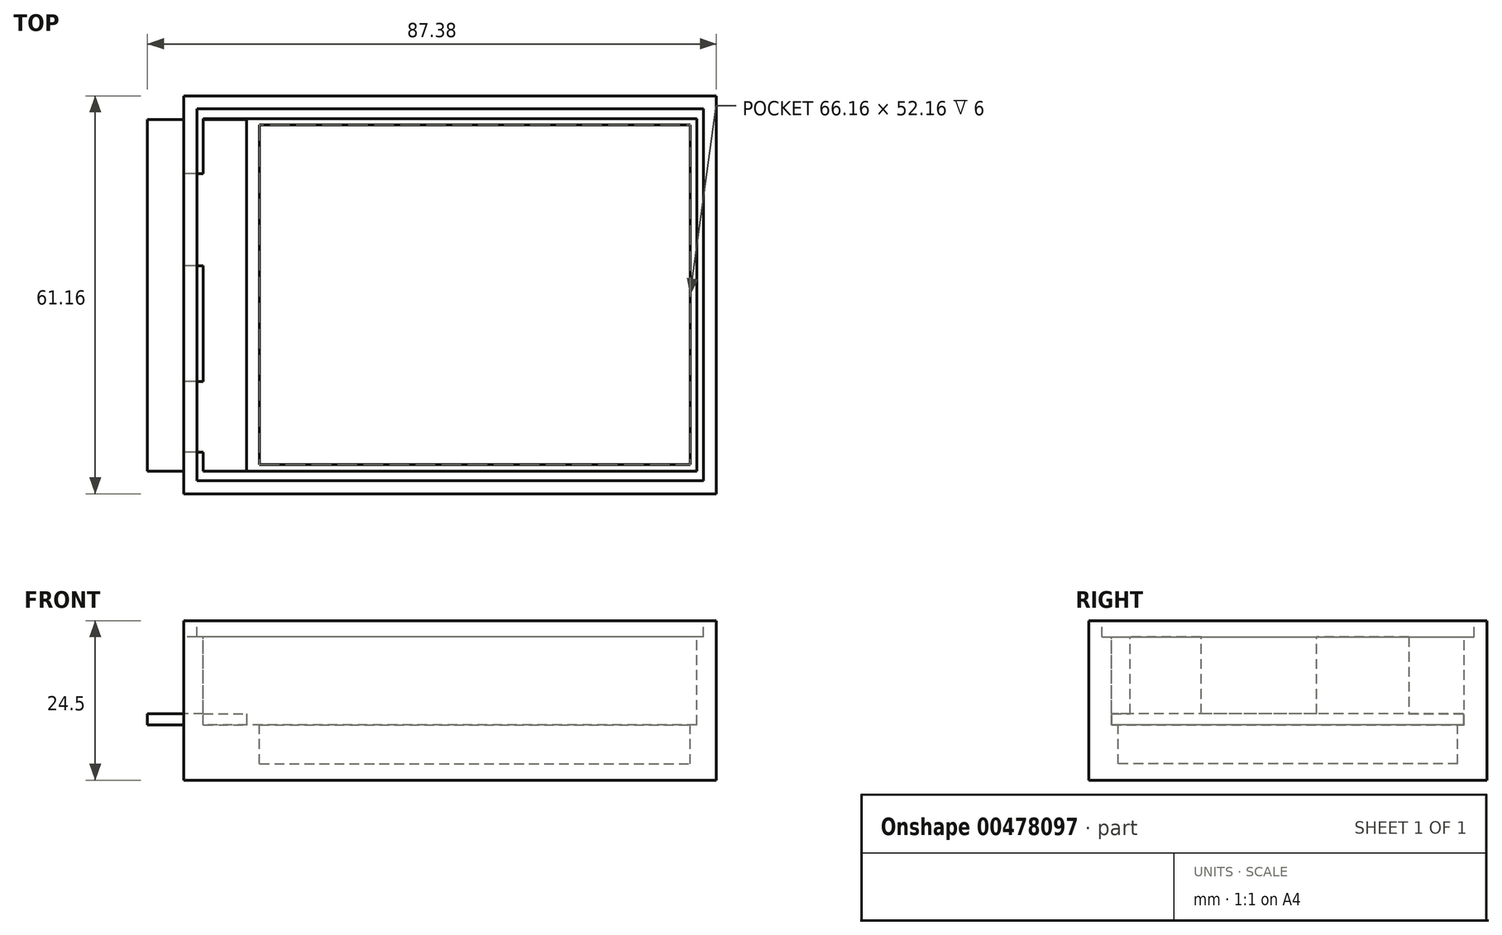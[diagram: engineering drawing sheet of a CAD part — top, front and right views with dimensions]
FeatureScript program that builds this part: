
annotation { "Feature Type Name" : "Feature", "Feature Type Description" : "" }
export const myFeature = defineFeature(function(context is Context, id is Id, definition is map)
    precondition{}
    {
        {
            var Q0;
            Q0=qCreatedBy(makeId("Top.planeOp"),FACE);
            var sketch = newSketch(context, id + "F0", { "sketchPlane" : qUnion([Q0])});
            skLineSegment(sketch, "E0.bottom", {"start": v(40.9, -30.58) * mm, "end": v(-40.9, -30.58) * mm});
            skLineSegment(sketch, "E0.top", {"start": v(40.9, 30.58) * mm, "end": v(-40.9, 30.58) * mm});
            skLineSegment(sketch, "E0.left", {"start": v(40.9, -30.58) * mm, "end": v(40.9, 30.58) * mm});
            skLineSegment(sketch, "E0.right", {"start": v(-40.9, -30.58) * mm, "end": v(-40.9, 30.58) * mm});
            skPoint(sketch, "E0.middle", {"position": v(0, 0) * mm});
            skLineSegment(sketch, "E1", {"start": v(-38.71, 81.8) * mm, "end": v(-38.71, -8.1) * mm, "construction": true});
            skLineSegment(sketch, "E2", {"start": v(-36.71, 83.32) * mm, "end": v(-36.71, -9.24) * mm, "construction": true});
            skLineSegment(sketch, "E3", {"start": v(-34.71, 80.3) * mm, "end": v(-34.71, -12.8) * mm, "construction": true});
            skSolve(sketch);
        }
        {
            var Q0;
            Q0 = qSketchRegion(id + "F0", true);
            extrude(context, id + "F1", {"entities" : qUnion([Q0]), "depth" : 24.5 * mm});
        }
        {
            var Q0;
            Q0=makeQuery(id+"F1.opExtrude","CAP_FACE",FACE,{"disambiguationData":[OSD([sQuery(id+"F0.wireOp",EDGE,"E0.bottom"),sQuery(id+"F0.wireOp",EDGE,"E0.top"),sQuery(id+"F0.wireOp",EDGE,"E0.left"),sQuery(id+"F0.wireOp",EDGE,"E0.right")])],"isStart":false});
            var sketch = newSketch(context, id + "F2", { "sketchPlane" : qUnion([Q0])});
            skLineSegment(sketch, "E4.bottom", {"start": v(38.9, -28.58) * mm, "end": v(-38.9, -28.58) * mm});
            skLineSegment(sketch, "E4.top", {"start": v(38.9, 28.58) * mm, "end": v(-38.9, 28.58) * mm});
            skLineSegment(sketch, "E4.left", {"start": v(38.9, -28.58) * mm, "end": v(38.9, 28.58) * mm});
            skLineSegment(sketch, "E4.right", {"start": v(-38.9, -28.58) * mm, "end": v(-38.9, 28.58) * mm});
            skPoint(sketch, "E4.middle", {"position": v(0, 0) * mm});
            skSolve(sketch);
        }
        {
            var Q0;
            Q0 = qSketchRegion(id + "F2", true);
            extrude(context, id + "F3", {"entities" : qUnion([Q0]), "operationType" : NewBodyOperationType.REMOVE, "oppositeDirection" : true, "depth" : 2.5 * mm});
        }
        {
            var Q0;
            Q0=makeQuery(id+"F3.boolean.opBoolean","COPY",FACE,{"derivedFrom":makeQuery(id+"F3.opExtrude","CAP_FACE",FACE,{"disambiguationData":[OSD([sQuery(id+"F2.wireOp",EDGE,"E4.bottom"),sQuery(id+"F2.wireOp",EDGE,"E4.top"),sQuery(id+"F2.wireOp",EDGE,"E4.left"),sQuery(id+"F2.wireOp",EDGE,"E4.right")])],"isStart":false})});
            var sketch = newSketch(context, id + "F4", { "sketchPlane" : qUnion([Q0])});
            skLineSegment(sketch, "E5.bottom", {"start": v(37.9, -27.08) * mm, "end": v(-37.9, -27.08) * mm});
            skLineSegment(sketch, "E5.top", {"start": v(37.9, 27.08) * mm, "end": v(-37.9, 27.08) * mm});
            skLineSegment(sketch, "E5.left", {"start": v(37.9, -27.08) * mm, "end": v(37.9, 27.08) * mm});
            skLineSegment(sketch, "E5.right", {"start": v(-37.9, -27.08) * mm, "end": v(-37.9, 27.08) * mm});
            skPoint(sketch, "E5.middle", {"position": v(0, 0) * mm});
            skSolve(sketch);
        }
        {
            var Q0;
            Q0 = qSketchRegion(id + "F4", true);
            extrude(context, id + "F5", {"entities" : qUnion([Q0]), "operationType" : NewBodyOperationType.REMOVE, "oppositeDirection" : true, "depth" : 13.5 * mm});
        }
        {
            var Q0;
            Q0=makeQuery(id+"F5.boolean.opBoolean","COPY",FACE,{"derivedFrom":makeQuery(id+"F5.opExtrude","CAP_FACE",FACE,{"disambiguationData":[OSD([sQuery(id+"F4.wireOp",EDGE,"E5.bottom"),sQuery(id+"F4.wireOp",EDGE,"E5.top"),sQuery(id+"F4.wireOp",EDGE,"E5.left"),sQuery(id+"F4.wireOp",EDGE,"E5.right")])],"isStart":false})});
            var sketch = newSketch(context, id + "F6", { "sketchPlane" : qUnion([Q0])});
            skLineSegment(sketch, "E6.bottom", {"start": v(-29.26, 26.08) * mm, "end": v(36.9, 26.08) * mm});
            skLineSegment(sketch, "E6.top", {"start": v(-29.26, -26.08) * mm, "end": v(36.9, -26.08) * mm});
            skLineSegment(sketch, "E6.left", {"start": v(-29.26, 26.08) * mm, "end": v(-29.26, -26.08) * mm});
            skLineSegment(sketch, "E6.right", {"start": v(36.9, 26.08) * mm, "end": v(36.9, -26.08) * mm});
            skLineSegment(sketch, "E7", {"start": v(-64.08, -24.87) * mm, "end": v(71.2, -24.87) * mm, "construction": true});
            skLineSegment(sketch, "E8", {"start": v(-58.28, 24.54) * mm, "end": v(66.4, 24.54) * mm, "construction": true});
            skSolve(sketch);
        }
        {
            var Q0;
            Q0 = qSketchRegion(id + "F6", true);
            extrude(context, id + "F7", {"entities" : qUnion([Q0]), "operationType" : NewBodyOperationType.REMOVE, "oppositeDirection" : true, "depth" : 6 * mm});
        }
        {
            var Q0;
            Q0=makeQuery(id+"F5.boolean.opBoolean","COPY",FACE,{"derivedFrom":makeQuery(id+"F5.opExtrude","CAP_FACE",FACE,{"disambiguationData":[OSD([sQuery(id+"F4.wireOp",EDGE,"E5.bottom"),sQuery(id+"F4.wireOp",EDGE,"E5.top"),sQuery(id+"F4.wireOp",EDGE,"E5.left"),sQuery(id+"F4.wireOp",EDGE,"E5.right")])],"isStart":false})});
            var sketch = newSketch(context, id + "F8", { "sketchPlane" : qUnion([Q0])});
            skLineSegment(sketch, "E9.bottom", {"start": v(-46.48, 26.92) * mm, "end": v(-31.26, 26.92) * mm});
            skLineSegment(sketch, "E9.top", {"start": v(-46.48, -27.1) * mm, "end": v(-31.26, -27.1) * mm});
            skLineSegment(sketch, "E9.left", {"start": v(-46.48, 26.92) * mm, "end": v(-46.48, -27.1) * mm});
            skLineSegment(sketch, "E9.right", {"start": v(-31.26, 26.92) * mm, "end": v(-31.26, -27.1) * mm});
            skSolve(sketch);
        }
        {
            var Q0;
            Q0 = qSketchRegion(id + "F8", true);
            extrude(context, id + "F9", {"entities" : qUnion([Q0]), "operationType" : NewBodyOperationType.ADD, "depth" : 1.7 * mm});
        }
        {
            var Q0;
            Q0=makeQuery(id+"F1.opExtrude","SWEPT_FACE",FACE,{"disambiguationData":[OSD([sQuery(id+"F0.wireOp",EDGE,"E0.right")])]});
            var sketch = newSketch(context, id + "F10", { "sketchPlane" : qUnion([Q0])});
            skLineSegment(sketch, "E10.bottom", {"start": v(-18.58, 22) * mm, "end": v(-4.42, 22) * mm});
            skLineSegment(sketch, "E10.top", {"start": v(-18.58, 10.2) * mm, "end": v(-4.42, 10.2) * mm});
            skLineSegment(sketch, "E10.left", {"start": v(-18.58, 22) * mm, "end": v(-18.58, 10.2) * mm});
            skLineSegment(sketch, "E10.right", {"start": v(-4.42, 22) * mm, "end": v(-4.42, 10.2) * mm});
            skLineSegment(sketch, "E11.bottom", {"start": v(13.32, 22) * mm, "end": v(24.22, 22) * mm});
            skLineSegment(sketch, "E11.top", {"start": v(13.32, 10.2) * mm, "end": v(24.22, 10.2) * mm});
            skLineSegment(sketch, "E11.left", {"start": v(13.32, 22) * mm, "end": v(13.32, 10.2) * mm});
            skLineSegment(sketch, "E11.right", {"start": v(24.22, 22) * mm, "end": v(24.22, 10.2) * mm});
            skSolve(sketch);
        }
        {
            var Q0;
            Q0=makeQuery(id+"F10.imprint","IMPRINT",FACE,{"disambiguationData":[TD([[makeQuery(id+"F10.imprint","IMPRINT",EDGE,{"derivedFrom":sQuery(id+"F10.wireOp",EDGE,"E10.bottom")}),-1.0]])]});
            var Q1;
            Q1=makeQuery(id+"F10.imprint","IMPRINT",FACE,{"disambiguationData":[TD([[makeQuery(id+"F10.imprint","IMPRINT",EDGE,{"derivedFrom":sQuery(id+"F10.wireOp",EDGE,"E11.bottom")}),-1.0]])]});
            extrude(context, id + "F11", {"entities" : qUnion([Q0, Q1]), "operationType" : NewBodyOperationType.REMOVE, "oppositeDirection" : true, "depth" : 4 * mm});
        }
    });
